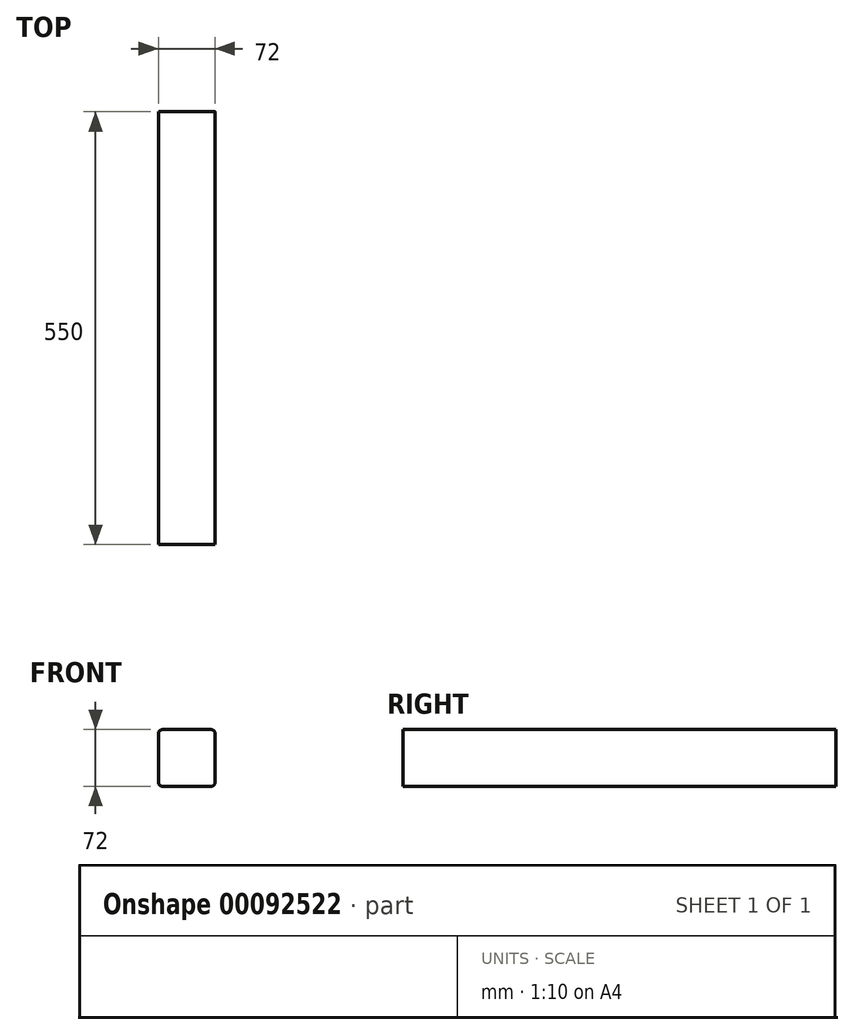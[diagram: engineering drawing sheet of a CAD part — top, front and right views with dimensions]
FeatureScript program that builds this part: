
annotation { "Feature Type Name" : "Feature", "Feature Type Description" : "" }
export const myFeature = defineFeature(function(context is Context, id is Id, definition is map)
    precondition{}
    {
        {
            var Q0;
            Q0=qCreatedBy(makeId("Front.planeOp"),FACE);
            var sketch = newSketch(context, id + "F0", { "sketchPlane" : qUnion([Q0])});
            skLineSegment(sketch, "E0.bottom", {"start": v(31, 36) * mm, "end": v(-31, 36) * mm});
            skLineSegment(sketch, "E0.top", {"start": v(31, -36) * mm, "end": v(-31, -36) * mm});
            skLineSegment(sketch, "E0.left", {"start": v(36, 31) * mm, "end": v(36, -31) * mm});
            skLineSegment(sketch, "E0.right", {"start": v(-36, 31) * mm, "end": v(-36, -31) * mm});
            skPoint(sketch, "E0.middle", {"position": v(0, 0) * mm});
            skPoint(sketch, "E1.visualSharp", {"position": v(-36, 36) * mm});
            skArc(sketch, "E1.filletArc", {"start": v(-31, 36) * mm, "mid": v(-34.54, 34.54) * mm, "end": v(-36, 31) * mm});
            skPoint(sketch, "E2.visualSharp", {"position": v(36, 36) * mm});
            skArc(sketch, "E2.filletArc", {"start": v(36, 31) * mm, "mid": v(34.54, 34.54) * mm, "end": v(31, 36) * mm});
            skPoint(sketch, "E3.visualSharp", {"position": v(36, -36) * mm});
            skArc(sketch, "E3.filletArc", {"start": v(31, -36) * mm, "mid": v(34.54, -34.54) * mm, "end": v(36, -31) * mm});
            skPoint(sketch, "E4.visualSharp", {"position": v(-36, -36) * mm});
            skArc(sketch, "E4.filletArc", {"start": v(-36, -31) * mm, "mid": v(-34.54, -34.54) * mm, "end": v(-31, -36) * mm});
            skSolve(sketch);
        }
        {
            var Q0;
            Q0=qSketchRegion(id+"F0",true);
            extrude(context, id + "F1", {"entities" : qUnion([Q0]), "depth" : 550 * mm});
        }
    });
